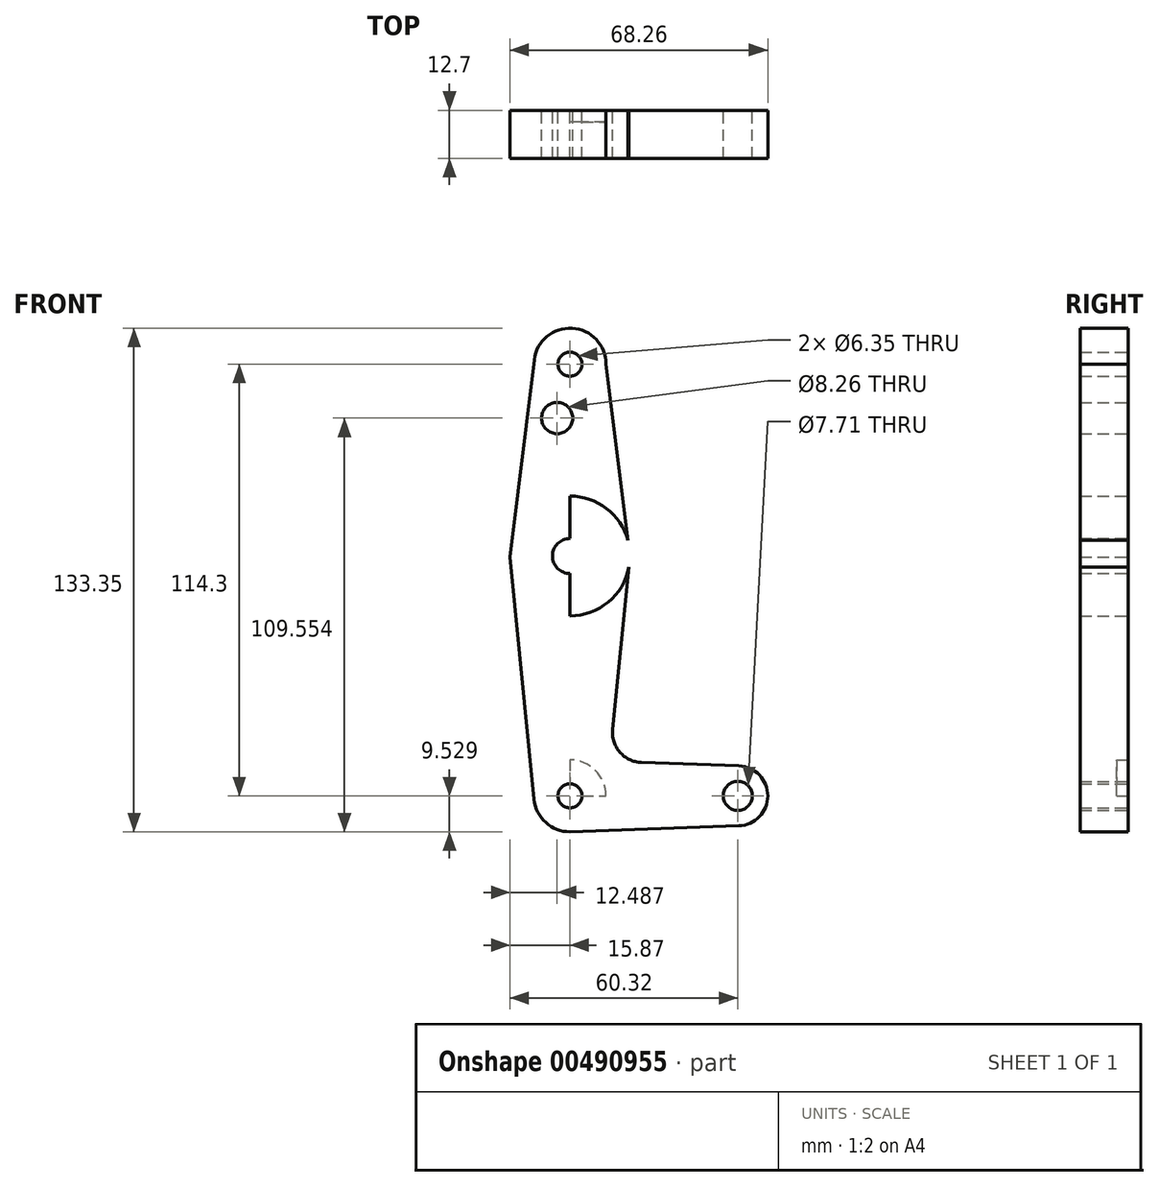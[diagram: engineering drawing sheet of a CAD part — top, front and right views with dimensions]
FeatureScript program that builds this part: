
annotation { "Feature Type Name" : "Feature", "Feature Type Description" : "" }
export const myFeature = defineFeature(function(context is Context, id is Id, definition is map)
    precondition{}
    {
        {
            var Q0;
            Q0=qCreatedBy(makeId("Front.planeOp"),FACE);
            var sketch = newSketch(context, id + "F0", { "sketchPlane" : qUnion([Q0])});
            skLineSegment(sketch, "E0", {"start": v(0, 63.13) * mm, "end": v(0, -51.17) * mm});
            skLineSegment(sketch, "E1", {"start": v(0, -51.17) * mm, "end": v(44.45, -51.17) * mm});
            skCircle(sketch, "E2", {"center": v(0, 63.13) * mm, "radius": 9.53 * mm});
            skCircle(sketch, "E3", {"center": v(0, 12.33) * mm, "radius": 15.88 * mm});
            skCircle(sketch, "E4", {"center": v(0, -51.17) * mm, "radius": 9.53 * mm});
            skCircle(sketch, "E5", {"center": v(44.45, -51.17) * mm, "radius": 7.94 * mm});
            skLineSegment(sketch, "E6", {"start": v(-9.45, 64.3) * mm, "end": v(-15.87, 12.07) * mm});
            skLineSegment(sketch, "E7", {"start": v(-15.87, 12.07) * mm, "end": v(-9.48, -52.12) * mm});
            skLineSegment(sketch, "E8", {"start": v(9.53, 63.13) * mm, "end": v(15.87, 12.07) * mm});
            skLineSegment(sketch, "E9", {"start": v(15.87, 12.07) * mm, "end": v(11.3, -33.58) * mm});
            skCircle(sketch, "E10", {"center": v(0, 63.13) * mm, "radius": 3.18 * mm});
            skCircle(sketch, "E11", {"center": v(-3.38, 48.85) * mm, "radius": 4.13 * mm});
            skCircle(sketch, "E12", {"center": v(0, 12.33) * mm, "radius": 4.63 * mm});
            skCircle(sketch, "E13", {"center": v(0, -51.17) * mm, "radius": 3.18 * mm});
            skCircle(sketch, "E14", {"center": v(44.45, -51.17) * mm, "radius": 3.85 * mm});
            skLineSegment(sketch, "E15", {"start": v(18.92, -42.32) * mm, "end": v(44.73, -43.24) * mm});
            skLineSegment(sketch, "E16", {"start": v(0, -60.7) * mm, "end": v(44.73, -59.1) * mm});
            skArc(sketch, "E17.filletArc", {"start": v(11.3, -33.58) * mm, "mid": v(13.21, -39.6) * mm, "end": v(18.92, -42.32) * mm});
            skSolve(sketch);
        }
        {
            var Q0;
            {var subQ1=sQuery(id+"F0.wireOp",EDGE,"E2");var subQ3=sQuery(id+"F0.wireOp",EDGE,"E0");var subQ4=makeQuery(id+"F0.imprint","INTERSECT",VERTEX,{"derivedFrom":[subQ3,subQ1]});Q0=makeQuery(id+"F0.imprint","IMPRINT",FACE,{"disambiguationData":[TD([[makeQuery(id+"F0.imprint","IMPRINT",EDGE,{"disambiguationData":[TD([[subQ4,-1.0]])],"derivedFrom":subQ3}),-1.0]])]});}
            var Q1;
            {var subQ3=sQuery(id+"F0.wireOp",EDGE,"E0");var subQ5=sQuery(id+"F0.wireOp",EDGE,"E2");var subQ7=makeQuery(id+"F0.imprint","INTERSECT",VERTEX,{"derivedFrom":[subQ3,subQ5]});Q1=makeQuery(id+"F0.imprint","IMPRINT",FACE,{"disambiguationData":[TD([[makeQuery(id+"F0.imprint","IMPRINT",EDGE,{"disambiguationData":[TD([[subQ7,-1.0]])],"derivedFrom":subQ3}),1.0]])]});}
            var Q2;
            Q2=makeQuery(id+"F0.imprint","IMPRINT",FACE,{"disambiguationData":[TD([[makeQuery(id+"F0.imprint","IMPRINT",EDGE,{"derivedFrom":sQuery(id+"F0.wireOp",EDGE,"E10")}),-1.0]])]});
            var Q3;
            {var subQ1=sQuery(id+"F0.wireOp",EDGE,"E3");var subQ3=sQuery(id+"F0.wireOp",EDGE,"E0");var subQ4=makeQuery(id+"F0.imprint","INTERSECT",VERTEX,{"disambiguationData":[OD(0.0)],"derivedFrom":[subQ3,subQ1]});Q3=makeQuery(id+"F0.imprint","IMPRINT",FACE,{"disambiguationData":[TD([[makeQuery(id+"F0.imprint","IMPRINT",EDGE,{"disambiguationData":[TD([[subQ4,-1.0]])],"derivedFrom":subQ3}),1.0]])]});}
            var Q4;
            {var subQ1=sQuery(id+"F0.wireOp",EDGE,"E3");var subQ3=sQuery(id+"F0.wireOp",EDGE,"E0");var subQ9=makeQuery(id+"F0.imprint","INTERSECT",VERTEX,{"disambiguationData":[OD(0.0)],"derivedFrom":[subQ3,subQ1]});Q4=makeQuery(id+"F0.imprint","IMPRINT",FACE,{"disambiguationData":[TD([[makeQuery(id+"F0.imprint","IMPRINT",EDGE,{"disambiguationData":[TD([[subQ9,-1.0]])],"derivedFrom":subQ3}),-1.0]])]});}
            var Q5;
            {var subQ0=sQuery(id+"F0.wireOp",EDGE,"E3");var subQ1=sQuery(id+"F0.wireOp",EDGE,"E0");var subQ2=makeQuery(id+"F0.imprint","INTERSECT",VERTEX,{"disambiguationData":[OD(1.0)],"derivedFrom":[subQ1,subQ0]});Q5=makeQuery(id+"F0.imprint","IMPRINT",FACE,{"disambiguationData":[TD([[makeQuery(id+"F0.imprint","IMPRINT",EDGE,{"disambiguationData":[TD([[subQ2,-1.0]])],"derivedFrom":subQ1}),-1.0]])]});}
            var Q6;
            {var subQ0=sQuery(id+"F0.wireOp",EDGE,"E4");var subQ4=sQuery(id+"F0.wireOp",EDGE,"E0");var subQ5=makeQuery(id+"F0.imprint","INTERSECT",VERTEX,{"derivedFrom":[subQ4,subQ0]});Q6=makeQuery(id+"F0.imprint","IMPRINT",FACE,{"disambiguationData":[TD([[makeQuery(id+"F0.imprint","IMPRINT",EDGE,{"disambiguationData":[TD([[subQ5,-1.0]])],"derivedFrom":subQ4}),-1.0]])]});}
            var Q7;
            {var subQ0=sQuery(id+"F0.wireOp",EDGE,"E4");var subQ1=sQuery(id+"F0.wireOp",EDGE,"E0");var subQ2=makeQuery(id+"F0.imprint","INTERSECT",VERTEX,{"derivedFrom":[subQ1,subQ0]});Q7=makeQuery(id+"F0.imprint","IMPRINT",FACE,{"disambiguationData":[TD([[makeQuery(id+"F0.imprint","IMPRINT",EDGE,{"disambiguationData":[TD([[subQ2,-1.0]])],"derivedFrom":subQ1}),1.0]])]});}
            var Q8;
            {var subQ5=sQuery(id+"F0.wireOp",EDGE,"E15");Q8=makeQuery(id+"F0.imprint","IMPRINT",FACE,{"disambiguationData":[TD([[makeQuery(id+"F0.imprint","IMPRINT",EDGE,{"derivedFrom":subQ5}),-1.0]])]});}
            var Q9;
            {var subQ0=sQuery(id+"F0.wireOp",EDGE,"E5");var subQ1=sQuery(id+"F0.wireOp",EDGE,"E1");var subQ2=makeQuery(id+"F0.imprint","INTERSECT",VERTEX,{"derivedFrom":[subQ1,subQ0]});Q9=makeQuery(id+"F0.imprint","IMPRINT",FACE,{"disambiguationData":[TD([[makeQuery(id+"F0.imprint","IMPRINT",EDGE,{"disambiguationData":[TD([[subQ2,1.0]])],"derivedFrom":subQ1}),-1.0]])]});}
            var Q10;
            Q10=makeQuery(id+"F0.imprint","IMPRINT",FACE,{"disambiguationData":[TD([[makeQuery(id+"F0.imprint","IMPRINT",EDGE,{"derivedFrom":sQuery(id+"F0.wireOp",EDGE,"E14")}),-1.0]])]});
            extrude(context, id + "F1", {"entities" : qUnion([Q0, Q1, Q2, Q3, Q4, Q5, Q6, Q7, Q8, Q9, Q10]), "depth" : 12.7 * mm});
        }
        {
            var Q0;
            {var subQ0=sQuery(id+"F0.wireOp",EDGE,"E4");var subQ1=sQuery(id+"F0.wireOp",EDGE,"E0");var subQ2=makeQuery(id+"F0.imprint","INTERSECT",VERTEX,{"derivedFrom":[subQ1,subQ0]});Q0=makeQuery(id+"F0.imprint","IMPRINT",FACE,{"disambiguationData":[TD([[makeQuery(id+"F0.imprint","IMPRINT",EDGE,{"disambiguationData":[TD([[subQ2,-1.0]])],"derivedFrom":subQ1}),1.0]])]});}
            extrude(context, id + "F2", {"entities" : qUnion([Q0]), "depth" : 3.05 * mm});
        }
    });
